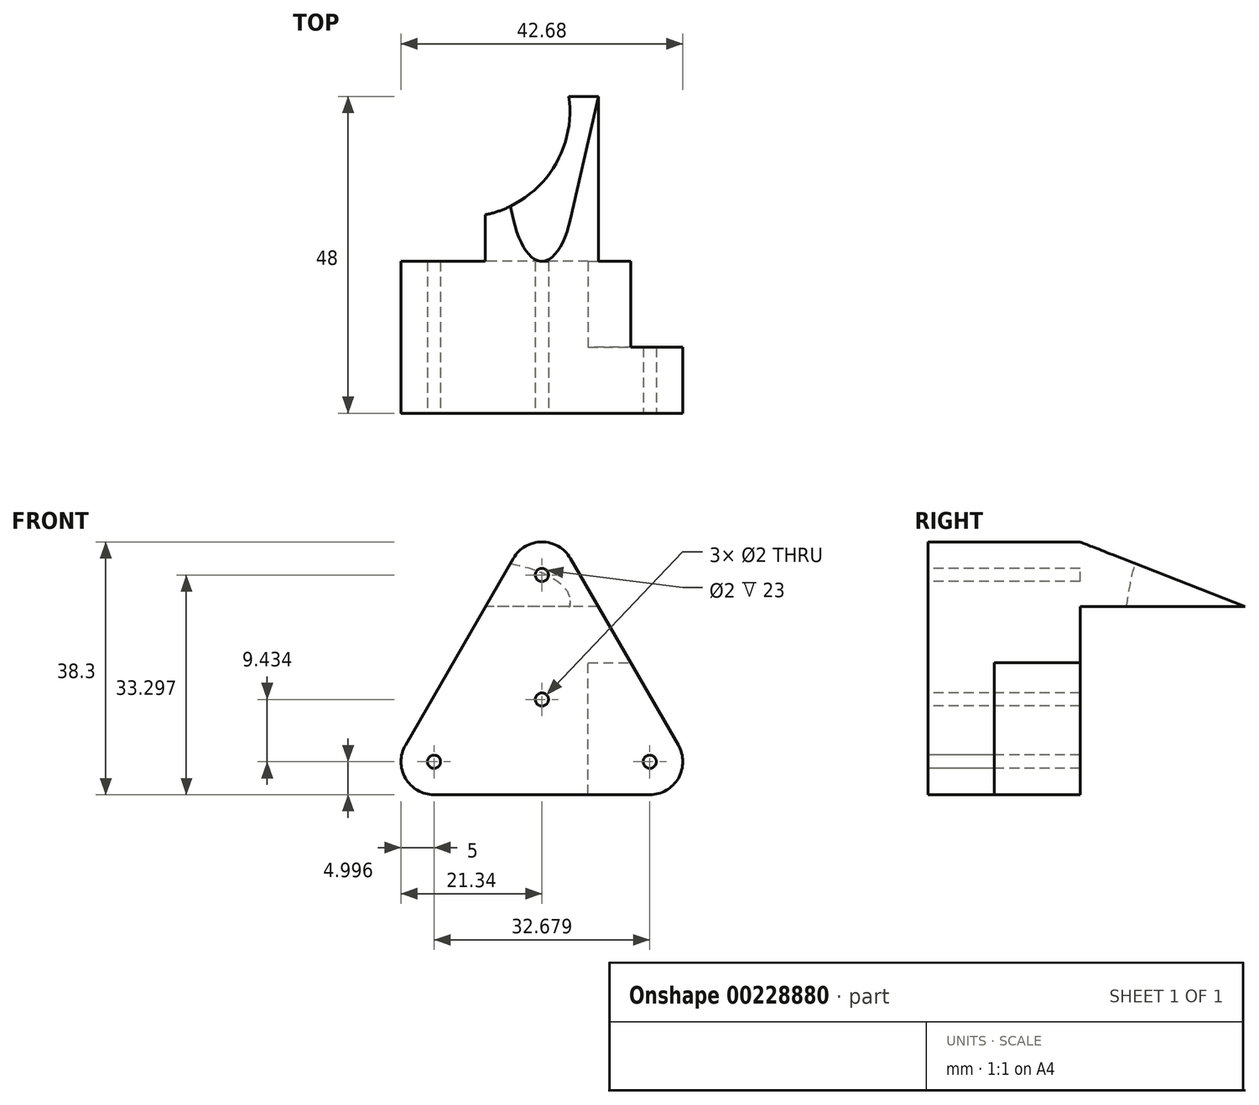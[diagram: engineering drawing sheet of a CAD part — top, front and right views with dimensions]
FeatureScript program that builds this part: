
annotation { "Feature Type Name" : "Feature", "Feature Type Description" : "" }
export const myFeature = defineFeature(function(context is Context, id is Id, definition is map)
    precondition{}
    {
        {
            var Q0;
            Q0=qCreatedBy(makeId("Front.planeOp"),FACE);
            var sketch = newSketch(context, id + "F0", { "sketchPlane" : qUnion([Q0])});
            skCircle(sketch, "E0", {"center": v(0, 0) * mm, "radius": 28.87 * mm, "construction": true});
            skLineSegment(sketch, "E1", {"start": v(-25, -14.43) * mm, "end": v(25, -14.43) * mm, "construction": true});
            skLineSegment(sketch, "E2", {"start": v(25, -14.43) * mm, "end": v(0, 28.87) * mm, "construction": true});
            skLineSegment(sketch, "E3", {"start": v(0, 28.87) * mm, "end": v(-25, -14.43) * mm, "construction": true});
            skCircle(sketch, "E4", {"center": v(-16.34, -9.43) * mm, "radius": 5 * mm, "construction": true});
            skCircle(sketch, "E5", {"center": v(0, 18.87) * mm, "radius": 5 * mm, "construction": true});
            skCircle(sketch, "E6", {"center": v(16.34, -9.43) * mm, "radius": 5 * mm, "construction": true});
            skLineSegment(sketch, "E7", {"start": v(-20.67, -6.93) * mm, "end": v(-4.33, 21.37) * mm});
            skLineSegment(sketch, "E8", {"start": v(4.33, 21.37) * mm, "end": v(20.67, -6.93) * mm});
            skLineSegment(sketch, "E9", {"start": v(16.34, -14.43) * mm, "end": v(-16.34, -14.43) * mm});
            skArc(sketch, "E10", {"start": v(-4.33, 21.37) * mm, "mid": v(0, 23.87) * mm, "end": v(4.33, 21.37) * mm});
            skArc(sketch, "E11", {"start": v(20.67, -6.93) * mm, "mid": v(20.67, -11.93) * mm, "end": v(16.34, -14.43) * mm});
            skArc(sketch, "E12", {"start": v(-16.34, -14.43) * mm, "mid": v(-20.67, -11.93) * mm, "end": v(-20.67, -6.93) * mm});
            skSolve(sketch);
        }
        {
            var Q0;
            Q0=makeQuery(id+"F0.imprint","IMPRINT",FACE,{"disambiguationData":[TD([[makeQuery(id+"F0.imprint","IMPRINT",EDGE,{"derivedFrom":sQuery(id+"F0.wireOp",EDGE,"E7")}),-1.0]])]});
            extrude(context, id + "F1", {"entities" : qUnion([Q0]), "depth" : 10 * mm});
        }
        {
            var Q0;
            Q0=makeQuery(id+"F1.opExtrude","CAP_FACE",FACE,{"disambiguationData":[OSD([sQuery(id+"F0.wireOp",EDGE,"E7"),sQuery(id+"F0.wireOp",EDGE,"E8"),sQuery(id+"F0.wireOp",EDGE,"E9"),sQuery(id+"F0.wireOp",EDGE,"E10"),sQuery(id+"F0.wireOp",EDGE,"E11"),sQuery(id+"F0.wireOp",EDGE,"E12")])],"isStart":false});
            var sketch = newSketch(context, id + "F2", { "sketchPlane" : qUnion([Q0])});
            skPoint(sketch, "E13", {"position": v(0, 18.87) * mm});
            skPoint(sketch, "E14", {"position": v(16.34, -9.43) * mm});
            skPoint(sketch, "E15", {"position": v(-16.34, -9.43) * mm});
            skPoint(sketch, "E16", {"position": v(0, 0) * mm});
            skSolve(sketch);
        }
        {
            var Q0;
            Q0=sQuery(id+"F2.wireOp",VERTEX,"E13");
            var Q1;
            Q1=sQuery(id+"F2.wireOp",VERTEX,"E16");
            var Q2;
            Q2=sQuery(id+"F2.wireOp",VERTEX,"E14");
            var Q3;
            Q3=sQuery(id+"F2.wireOp",VERTEX,"E15");
            var Q4;
            Q4=makeQuery(id+"F1.opExtrude","SWEPT_BODY",BODY,{"disambiguationData":[OSD([sQuery(id+"F0.wireOp",EDGE,"E7"),sQuery(id+"F0.wireOp",EDGE,"E8"),sQuery(id+"F0.wireOp",EDGE,"E9"),sQuery(id+"F0.wireOp",EDGE,"E10"),sQuery(id+"F0.wireOp",EDGE,"E11"),sQuery(id+"F0.wireOp",EDGE,"E12")])]});
            hole(context, id + "F3", {"style" : HoleStyle.SIMPLE, "endStyle" : HoleEndStyle.BLIND, "holeDiameter" : 2 * mm, "holeDepth" : 12 * mm, "locations" : qUnion([Q0, Q1, Q2, Q3]), "scope" : qUnion([Q4])});
        }
        {
            var Q0;
            Q0=makeQuery(id+"F1.opExtrude","CAP_FACE",FACE,{"disambiguationData":[OSD([sQuery(id+"F0.wireOp",EDGE,"E7"),sQuery(id+"F0.wireOp",EDGE,"E8"),sQuery(id+"F0.wireOp",EDGE,"E9"),sQuery(id+"F0.wireOp",EDGE,"E10"),sQuery(id+"F0.wireOp",EDGE,"E11"),sQuery(id+"F0.wireOp",EDGE,"E12")])],"isStart":true});
            var sketch = newSketch(context, id + "F4", { "sketchPlane" : qUnion([Q0])});
            skLineSegment(sketch, "E17", {"start": v(33, -14.43) * mm, "end": v(-7, -14.43) * mm, "construction": true});
            skLineSegment(sketch, "E18", {"start": v(-7, -14.43) * mm, "end": v(-7, 5.57) * mm});
            skLineSegment(sketch, "E19", {"start": v(-7, 5.57) * mm, "end": v(-33, 5.57) * mm, "construction": true});
            skLineSegment(sketch, "E20", {"start": v(-33, 5.57) * mm, "end": v(-33, 0) * mm, "construction": true});
            skLineSegment(sketch, "E21", {"start": v(-33, 0) * mm, "end": v(0, 0) * mm, "construction": true});
            skLineSegment(sketch, "E22", {"start": v(0, 0) * mm, "end": v(33, 0) * mm, "construction": true});
            skLineSegment(sketch, "E23", {"start": v(33, 0) * mm, "end": v(33, -14.43) * mm, "construction": true});
            skArc(sketch, "E24.0.0", {"start": v(-20.67, -6.93) * mm, "mid": v(-20.67, -11.93) * mm, "end": v(-16.34, -14.43) * mm, "construction": true});
            skLineSegment(sketch, "E24.0.1", {"start": v(-16.34, -14.43) * mm, "end": v(16.34, -14.43) * mm, "construction": true});
            skArc(sketch, "E24.0.2", {"start": v(16.34, -14.43) * mm, "mid": v(20.67, -11.93) * mm, "end": v(20.67, -6.93) * mm});
            skLineSegment(sketch, "E24.0.3", {"start": v(20.67, -6.93) * mm, "end": v(4.33, 21.37) * mm, "construction": true});
            skArc(sketch, "E24.0.4", {"start": v(4.33, 21.37) * mm, "mid": v(0, 23.87) * mm, "end": v(-4.33, 21.37) * mm});
            skLineSegment(sketch, "E24.0.5", {"start": v(-4.33, 21.37) * mm, "end": v(-20.67, -6.93) * mm, "construction": true});
            skLineSegment(sketch, "E25", {"start": v(-13.45, 5.57) * mm, "end": v(-4.33, 21.37) * mm});
            skLineSegment(sketch, "E26", {"start": v(4.33, 21.37) * mm, "end": v(20.67, -6.93) * mm});
            skLineSegment(sketch, "E27", {"start": v(16.34, -14.43) * mm, "end": v(-7, -14.43) * mm});
            skLineSegment(sketch, "E28", {"start": v(-7, 5.57) * mm, "end": v(-13.45, 5.57) * mm});
            skSolve(sketch);
        }
        {
            var Q0;
            Q0=makeQuery(id+"F4.imprint","IMPRINT",FACE,{"disambiguationData":[TD([[makeQuery(id+"F4.imprint","IMPRINT",EDGE,{"derivedFrom":sQuery(id+"F4.wireOp",EDGE,"E18")}),-1.0]])]});
            var Q1;
            Q1=makeQuery(id+"F4.imprint","IMPRINT",FACE,{"disambiguationData":[TD([[makeQuery(id+"F4.imprint","IMPRINT",EDGE,{"derivedFrom":makeQuery(id+"F3.hole-0.boolean.opBoolean","INTERSECT",EDGE,{"derivedFrom":[makeQuery(id+"F1.opExtrude","CAP_FACE",FACE,{"disambiguationData":[OSD([sQuery(id+"F0.wireOp",EDGE,"E7"),sQuery(id+"F0.wireOp",EDGE,"E8"),sQuery(id+"F0.wireOp",EDGE,"E9"),sQuery(id+"F0.wireOp",EDGE,"E10"),sQuery(id+"F0.wireOp",EDGE,"E11"),sQuery(id+"F0.wireOp",EDGE,"E12")])],"isStart":true}),makeQuery(id+"F3.hole-0.opRevolve","SWEPT_FACE",FACE,{"disambiguationData":[OSD([sQuery(id+"F3.hole-0.sketch.wireOp",EDGE,"core_line_2")])]})]})}),1.0]])]});
            var Q2;
            Q2=makeQuery(id+"F4.imprint","IMPRINT",FACE,{"disambiguationData":[TD([[makeQuery(id+"F4.imprint","IMPRINT",EDGE,{"derivedFrom":makeQuery(id+"F3.hole-1.boolean.opBoolean","INTERSECT",EDGE,{"derivedFrom":[makeQuery(id+"F1.opExtrude","CAP_FACE",FACE,{"disambiguationData":[OSD([sQuery(id+"F0.wireOp",EDGE,"E7"),sQuery(id+"F0.wireOp",EDGE,"E8"),sQuery(id+"F0.wireOp",EDGE,"E9"),sQuery(id+"F0.wireOp",EDGE,"E10"),sQuery(id+"F0.wireOp",EDGE,"E11"),sQuery(id+"F0.wireOp",EDGE,"E12")])],"isStart":true}),makeQuery(id+"F3.hole-1.opRevolve","SWEPT_FACE",FACE,{"disambiguationData":[OSD([sQuery(id+"F3.hole-1.sketch.wireOp",EDGE,"core_line_2")])]})]})}),1.0]])]});
            var Q3;
            Q3=makeQuery(id+"F4.imprint","IMPRINT",FACE,{"disambiguationData":[TD([[makeQuery(id+"F4.imprint","IMPRINT",EDGE,{"derivedFrom":makeQuery(id+"F3.hole-3.boolean.opBoolean","INTERSECT",EDGE,{"derivedFrom":[makeQuery(id+"F1.opExtrude","CAP_FACE",FACE,{"disambiguationData":[OSD([sQuery(id+"F0.wireOp",EDGE,"E7"),sQuery(id+"F0.wireOp",EDGE,"E8"),sQuery(id+"F0.wireOp",EDGE,"E9"),sQuery(id+"F0.wireOp",EDGE,"E10"),sQuery(id+"F0.wireOp",EDGE,"E11"),sQuery(id+"F0.wireOp",EDGE,"E12")])],"isStart":true}),makeQuery(id+"F3.hole-3.opRevolve","SWEPT_FACE",FACE,{"disambiguationData":[OSD([sQuery(id+"F3.hole-3.sketch.wireOp",EDGE,"core_line_2")])]})]})}),1.0]])]});
            extrude(context, id + "F5", {"entities" : qUnion([Q0, Q1, Q2, Q3]), "operationType" : NewBodyOperationType.ADD, "depth" : 13 * mm});
        }
        {
            var Q0;
            Q0=makeQuery(id+"F5.opExtrude","CAP_FACE",FACE,{"disambiguationData":[OSD([sQuery(id+"F4.wireOp",EDGE,"E18"),sQuery(id+"F4.wireOp",EDGE,"E24.0.2"),sQuery(id+"F4.wireOp",EDGE,"E24.0.4"),sQuery(id+"F4.wireOp",EDGE,"E25"),sQuery(id+"F4.wireOp",EDGE,"E26"),sQuery(id+"F4.wireOp",EDGE,"E27"),sQuery(id+"F4.wireOp",EDGE,"E28")])],"isStart":false});
            var sketch = newSketch(context, id + "F6", { "sketchPlane" : qUnion([Q0])});
            skLineSegment(sketch, "E29.0.0", {"start": v(-13.45, 5.57) * mm, "end": v(-7, 5.57) * mm, "construction": true});
            skLineSegment(sketch, "E29.0.1", {"start": v(-7, 5.57) * mm, "end": v(-7, -14.43) * mm, "construction": true});
            skLineSegment(sketch, "E29.0.2", {"start": v(-7, -14.43) * mm, "end": v(16.34, -14.43) * mm, "construction": true});
            skArc(sketch, "E29.0.3", {"start": v(16.34, -14.43) * mm, "mid": v(20.67, -11.93) * mm, "end": v(20.67, -6.93) * mm, "construction": true});
            skLineSegment(sketch, "E29.0.4", {"start": v(20.67, -6.93) * mm, "end": v(4.33, 21.37) * mm, "construction": true});
            skArc(sketch, "E29.0.5", {"start": v(4.33, 21.37) * mm, "mid": v(0, 23.87) * mm, "end": v(-4.33, 21.37) * mm});
            skLineSegment(sketch, "E29.0.6", {"start": v(-4.33, 21.37) * mm, "end": v(-13.45, 5.57) * mm, "construction": true});
            skLineSegment(sketch, "E30", {"start": v(-8.55, 14.07) * mm, "end": v(8.55, 14.07) * mm});
            skLineSegment(sketch, "E31", {"start": v(-8.55, 14.07) * mm, "end": v(-4.33, 21.37) * mm});
            skLineSegment(sketch, "E32", {"start": v(8.55, 14.07) * mm, "end": v(4.33, 21.37) * mm});
            skSolve(sketch);
        }
        {
            var Q0;
            Q0 = qSketchRegion(id + "F6", true);
            extrude(context, id + "F7", {"entities" : qUnion([Q0]), "operationType" : NewBodyOperationType.ADD, "depth" : 25 * mm});
        }
        {
            var Q0;
            Q0=makeQuery(id+"F7.opExtrude","SWEPT_FACE",FACE,{"disambiguationData":[OSD([sQuery(id+"F6.wireOp",EDGE,"E30")])]});
            var sketch = newSketch(context, id + "F8", { "sketchPlane" : qUnion([Q0])});
            skCircle(sketch, "E33", {"center": v(-11.75, -35.75) * mm, "radius": 16 * mm});
            skSolve(sketch);
        }
        {
            var Q0;
            {var subQ0=sQuery(id+"F8.wireOp",EDGE,"E33");var subQ1=sQuery(id+"F6.wireOp",EDGE,"E30");var subQ4=makeQuery(id+"F7.opExtrude","CAP_EDGE",EDGE,{"disambiguationData":[OSD([subQ1])],"isStart":false});var subQ5=makeQuery(id+"F8.imprint","INTERSECT",VERTEX,{"derivedFrom":[subQ4,subQ0]});Q0=makeQuery(id+"F8.imprint","IMPRINT",FACE,{"disambiguationData":[TD([[makeQuery(id+"F8.imprint","IMPRINT",EDGE,{"disambiguationData":[TD([[subQ5,1.0]])],"derivedFrom":subQ0}),1.0]])]});}
            var Q1;
            {var subQ0=sQuery(id+"F8.wireOp",EDGE,"E33");var subQ1=sQuery(id+"F6.wireOp",EDGE,"E30");var subQ4=makeQuery(id+"F7.opExtrude","CAP_EDGE",EDGE,{"disambiguationData":[OSD([subQ1])],"isStart":false});var subQ5=makeQuery(id+"F8.imprint","INTERSECT",VERTEX,{"derivedFrom":[subQ4,subQ0]});Q1=makeQuery(id+"F8.imprint","IMPRINT",FACE,{"disambiguationData":[TD([[makeQuery(id+"F8.imprint","IMPRINT",EDGE,{"disambiguationData":[TD([[subQ5,-1.0]])],"derivedFrom":subQ0}),1.0]])]});}
            extrude(context, id + "F9", {"entities" : qUnion([Q0, Q1]), "operationType" : NewBodyOperationType.REMOVE, "endBound" : BoundingType.THROUGH_ALL, "oppositeDirection" : true, "depth" : 25 * mm});
        }
        {
            var Q0;
            Q0=qCreatedBy(makeId("Right.planeOp"),FACE);
            var sketch = newSketch(context, id + "F10", { "sketchPlane" : qUnion([Q0])});
            skPoint(sketch, "E34.0", {"position": v(38, 14.07) * mm});
            skLineSegment(sketch, "E35.0", {"start": v(13, -6.93) * mm, "end": v(13, 14.07) * mm, "construction": true});
            skLineSegment(sketch, "E36", {"start": v(38, 14.07) * mm, "end": v(13, 23.87) * mm});
            skLineSegment(sketch, "E37", {"start": v(13, 23.87) * mm, "end": v(13, 24.87) * mm});
            skLineSegment(sketch, "E38", {"start": v(13, 24.87) * mm, "end": v(39, 24.87) * mm});
            skLineSegment(sketch, "E39", {"start": v(39, 24.87) * mm, "end": v(39, 14.07) * mm});
            skLineSegment(sketch, "E40", {"start": v(39, 14.07) * mm, "end": v(38, 14.07) * mm});
            skSolve(sketch);
        }
        {
            var Q0;
            Q0=makeQuery(id+"F10.imprint","IMPRINT",FACE,{"disambiguationData":[TD([[makeQuery(id+"F10.imprint","IMPRINT",EDGE,{"derivedFrom":sQuery(id+"F10.wireOp",EDGE,"E36")}),-1.0]])]});
            extrude(context, id + "F11", {"entities" : qUnion([Q0]), "operationType" : NewBodyOperationType.REMOVE, "endBound" : BoundingType.SYMMETRIC, "oppositeDirection" : true, "depth" : 25 * mm});
        }
    });
